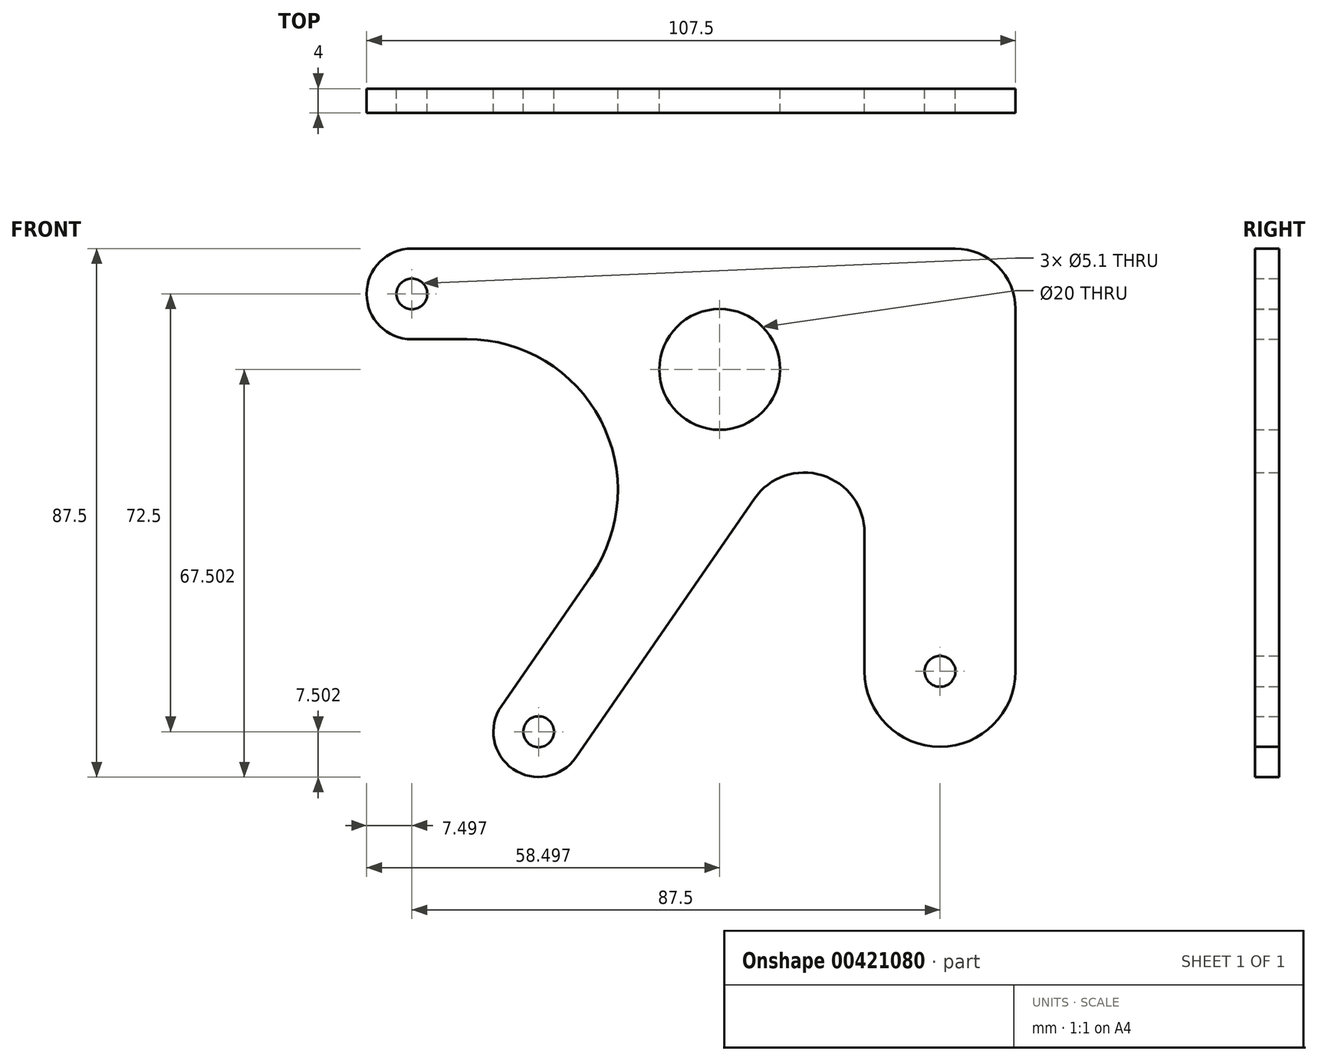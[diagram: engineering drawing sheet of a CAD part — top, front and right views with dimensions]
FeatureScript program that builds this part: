
annotation { "Feature Type Name" : "Feature", "Feature Type Description" : "" }
export const myFeature = defineFeature(function(context is Context, id is Id, definition is map)
    precondition{}
    {
        {
            var Q0;
            Q0=qCreatedBy(makeId("Front.planeOp"),FACE);
            var sketch = newSketch(context, id + "F0", { "sketchPlane" : qUnion([Q0])});
            skLineSegment(sketch, "E0", {"start": v(-54.77, 45.57) * mm, "end": v(35.23, 45.57) * mm});
            skLineSegment(sketch, "E1", {"start": v(45.23, 35.57) * mm, "end": v(45.23, -24.43) * mm});
            skLineSegment(sketch, "E2", {"start": v(20.23, -24.43) * mm, "end": v(20.23, -1.5) * mm});
            skLineSegment(sketch, "E3", {"start": v(2, 4.17) * mm, "end": v(-27.6, -38.7) * mm});
            skLineSegment(sketch, "E4", {"start": v(-39.94, -30.17) * mm, "end": v(-25.08, -8.63) * mm});
            skLineSegment(sketch, "E5", {"start": v(-45.65, 30.57) * mm, "end": v(-54.77, 30.57) * mm});
            skCircle(sketch, "E6", {"center": v(-54.77, 38.07) * mm, "radius": 2.55 * mm});
            skPoint(sketch, "E6.centerSnap0", {"position": v(-60.6, 38.07) * mm});
            skCircle(sketch, "E7", {"center": v(32.73, -24.43) * mm, "radius": 2.55 * mm});
            skCircle(sketch, "E8", {"center": v(-33.77, -34.43) * mm, "radius": 2.55 * mm});
            skArc(sketch, "E9", {"start": v(-54.77, 45.57) * mm, "mid": v(-62.27, 38.07) * mm, "end": v(-54.77, 30.57) * mm});
            skArc(sketch, "E10", {"start": v(-39.94, -30.17) * mm, "mid": v(-38.04, -40.6) * mm, "end": v(-27.6, -38.7) * mm});
            skArc(sketch, "E11", {"start": v(20.23, -24.43) * mm, "mid": v(32.73, -36.93) * mm, "end": v(45.23, -24.43) * mm});
            skPoint(sketch, "E12.trimOffspring.end.orphan", {"position": v(-60.6, 45.57) * mm});
            skPoint(sketch, "E13.start.orphan", {"position": v(-60.6, 30.57) * mm});
            skPoint(sketch, "E14.visualSharp", {"position": v(20.23, 30.57) * mm});
            skArc(sketch, "E14.filletArc", {"start": v(20.23, -1.5) * mm, "mid": v(13.2, 8.04) * mm, "end": v(2, 4.17) * mm});
            skCircle(sketch, "E15", {"center": v(-3.77, 25.57) * mm, "radius": 10 * mm});
            skPoint(sketch, "E16.visualSharp", {"position": v(45.23, 45.57) * mm});
            skArc(sketch, "E16.filletArc", {"start": v(45.23, 35.57) * mm, "mid": v(42.3, 42.64) * mm, "end": v(35.23, 45.57) * mm});
            skPoint(sketch, "E17.visualSharp", {"position": v(2, 30.57) * mm});
            skArc(sketch, "E17.filletArc", {"start": v(-25.08, -8.63) * mm, "mid": v(-23.5, 17.19) * mm, "end": v(-45.65, 30.57) * mm});
            skSolve(sketch);
        }
        {
            var Q0;
            Q0 = qSketchRegion(id + "F0", true);
            extrude(context, id + "F1", {"entities" : qUnion([Q0]), "depth" : 4 * mm});
        }
    });
